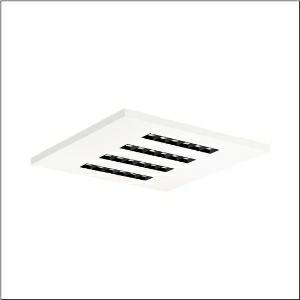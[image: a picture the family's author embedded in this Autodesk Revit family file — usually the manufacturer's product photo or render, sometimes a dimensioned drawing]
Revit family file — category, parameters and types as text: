
# Revit family: silica_r__21_square_51mx6kds34w_2a5b
name_source: partatom
category: Lighting Fixtures
units: mm (PartAtom-declared; Revit-internal decimal feet)

## family parameters
Cut with Voids When Loaded = No
Host = Face
Light Source = No
Part Type = Normal
Room Calculation Point = No
Round Connector Dimension = Use Diameter
Shared = No

## types (1)
- --- (1 x LED, 4600 lm, 31.9 W, 3000K)
    Apparent Load = 32 VA
    CIE Flux Codes = 86 100 100 100 100
    Color Rendering = 80
    Color Temperature = 3000K
    Default Elevation = 1800 mm
    Description = Silica® 21 Square, office luminaire, primary light control with lens, of PMMA, primary anti-glare with reflector, of PC, black, CAT 2 (L<= 3000cd/m²), light emission: direct distribution, primary light characteristic: symmetric, installation type: lay-in mounting, LED, rated luminous flux: 4.600lm, luminous efficacy: 144lm/W, light colour: 830, colour temperature: 3000K, control gear: DALI 2, with terminal, 5-pole, mains connection: 220..240V, AC, 50/60Hz, rated input power: 31.9W, luminaire housing, of sheet steel, coated, traffic white (RAL 9016), module: M600, length: 597mm, width: 597mm, height: 33mm, protection rating (complete): IP20, insulation class (complete): insulation class I (protective earthing), certification: CE, ENEC, VDE, permissible operating ambient temperature: -20..+40°C, standard: EN 50419, packaging unit: 1 piece
    Height = 0 mm  [stored 0 ft]
    Lamp = 1 x LED
    Lamp Light Flux = 4600 lm
    Lamp Power = 31.9 W
    Lamp count = 1
    Length = 597 mm
    Luminous efficacy = 144 lm/W
    Manufacturer = Siteco
    ModVariant = No
    Model = 51MX6KDS34W
    Mounting Place = Ceiling
    Mounting Type = Recessed
    Number of Poles = 1
    OnlyDefault = Yes
    Power Factor = 1
    Product Name = Silica® 21 Square
    Product group = office luminaire | ceiling recessed
    ProductGroupID = 401
    Protection Class = Protection class I
    Protection Degree = IP 20
    RLX_Detail_Level = 1
    RLX_Emergency_Light_Flux = 0 lm
    RLX_Emergency_Type = 0
    RLX_Emergency_Type_DB = No
    RlxData = <blob elided: 21113 chars, md5=91206b12>
    Socket = socket
    Standby Power = 0 W
    System Light Flux = 4600 lm
    System Power = 32 W
    Type Comments = factory setting: luminous flux: 100 % | dim-lin: 254 | 430 mA
    Type Image = l_1275207.jpg
    URL = http://relux.com
    VarID = @adj_084076
    Voltage = 0 V
    Weight = 0.00 kg
    Width = 597 mm

note: [stored X ft] marks values corroborated as IEEE doubles in the binary element streams (Revit-internal decimal feet)

## geometry (parser evidence)
native form markers: Blend x4, Sweep x11
no freeform markers — native parametric forms only
